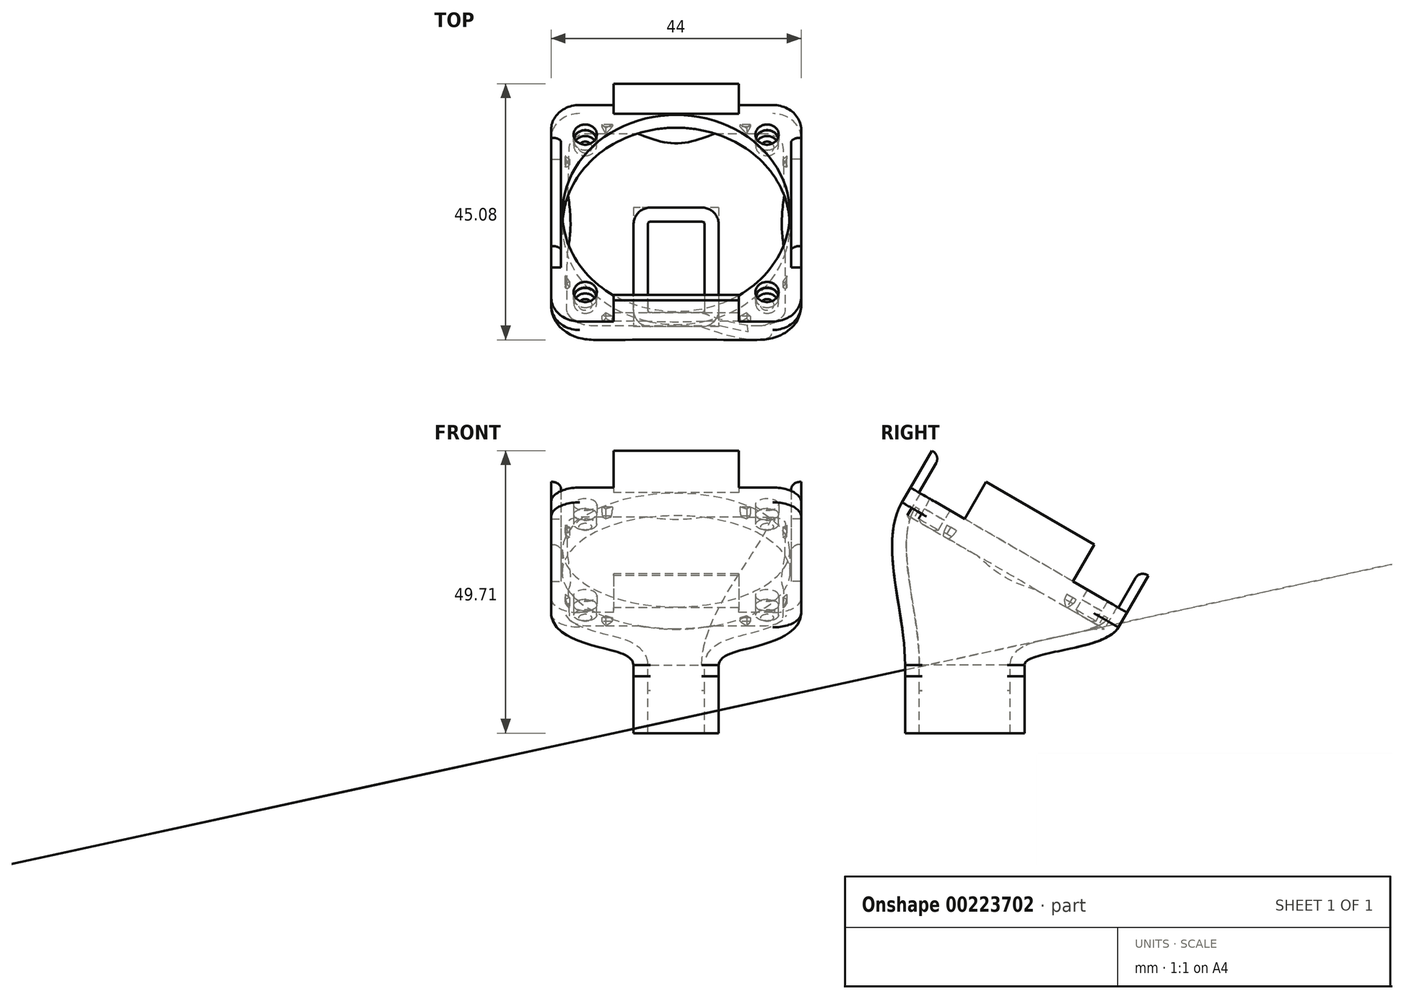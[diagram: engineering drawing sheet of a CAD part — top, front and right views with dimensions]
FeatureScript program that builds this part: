
annotation { "Feature Type Name" : "Feature", "Feature Type Description" : "" }
export const myFeature = defineFeature(function(context is Context, id is Id, definition is map)
    precondition{}
    {
        {
            var Q0;
            Q0=qCreatedBy(makeId("Top.planeOp"),FACE);
            var sketch = newSketch(context, id + "F17", { "sketchPlane" : qUnion([Q0])});
            skLineSegment(sketch, "E0.bottom", {"start": v(7.5, 10.5) * mm, "end": v(-7.5, 10.5) * mm});
            skLineSegment(sketch, "E0.top", {"start": v(7.5, -10.5) * mm, "end": v(-7.5, -10.5) * mm});
            skLineSegment(sketch, "E0.left", {"start": v(7.5, 10.5) * mm, "end": v(7.5, -10.5) * mm});
            skLineSegment(sketch, "E0.right", {"start": v(-7.5, 10.5) * mm, "end": v(-7.5, -10.5) * mm});
            skPoint(sketch, "E0.middle", {"position": v(0, 0) * mm});
            skSolve(sketch);
        }
        {
            var Q0;
            Q0=makeQuery(id+"F17.imprint","IMPRINT",FACE,{"disambiguationData":[TD([[makeQuery(id+"F17.imprint","IMPRINT",EDGE,{"derivedFrom":sQuery(id+"F17.wireOp",EDGE,"E0.bottom")}),1.0]])]});
            extrude(context, id + "F18", {"entities" : qUnion([Q0]), "oppositeDirection" : true, "depth" : 10 * mm});
        }
        {
            var Q0;
            Q0=makeQuery(id+"F18.opExtrude","CAP_FACE",FACE,{"disambiguationData":[OSD([sQuery(id+"F17.wireOp",EDGE,"E0.bottom"),sQuery(id+"F17.wireOp",EDGE,"E0.top"),sQuery(id+"F17.wireOp",EDGE,"E0.left"),sQuery(id+"F17.wireOp",EDGE,"E0.right"),sQuery(id+"F17.wireOp",EDGE,"fad1de10-4d12-4315-86bb-0567689870b4.bottom"),sQuery(id+"F17.wireOp",EDGE,"fad1de10-4d12-4315-86bb-0567689870b4.top"),sQuery(id+"F17.wireOp",EDGE,"fad1de10-4d12-4315-86bb-0567689870b4.left"),sQuery(id+"F17.wireOp",EDGE,"fad1de10-4d12-4315-86bb-0567689870b4.right")])],"isStart":true});
            var sketch = newSketch(context, id + "F0", { "sketchPlane" : qUnion([Q0])});
            skPoint(sketch, "E1.middle", {"position": v(0, 0) * mm});
            skLineSegment(sketch, "E2.bottom", {"start": v(-4.5, -10.5) * mm, "end": v(4.5, -10.5) * mm});
            skLineSegment(sketch, "E2.top", {"start": v(-4.5, 10.5) * mm, "end": v(4.5, 10.5) * mm});
            skLineSegment(sketch, "E2.left", {"start": v(-7.5, -7.5) * mm, "end": v(-7.5, 7.5) * mm});
            skLineSegment(sketch, "E2.right", {"start": v(7.5, -7.5) * mm, "end": v(7.5, 7.5) * mm});
            skPoint(sketch, "E3.visualSharp", {"position": v(-7.5, -10.5) * mm});
            skArc(sketch, "E3.filletArc", {"start": v(-7.5, -7.5) * mm, "mid": v(-6.62, -9.62) * mm, "end": v(-4.5, -10.5) * mm});
            skPoint(sketch, "E4.visualSharp", {"position": v(7.5, -10.5) * mm});
            skArc(sketch, "E4.filletArc", {"start": v(4.5, -10.5) * mm, "mid": v(6.62, -9.62) * mm, "end": v(7.5, -7.5) * mm});
            skPoint(sketch, "E5.visualSharp", {"position": v(7.5, 10.5) * mm});
            skArc(sketch, "E5.filletArc", {"start": v(7.5, 7.5) * mm, "mid": v(6.62, 9.62) * mm, "end": v(4.5, 10.5) * mm});
            skPoint(sketch, "E6.visualSharp", {"position": v(-7.5, 10.5) * mm});
            skArc(sketch, "E6.filletArc", {"start": v(-4.5, 10.5) * mm, "mid": v(-6.62, 9.62) * mm, "end": v(-7.5, 7.5) * mm});
            skSolve(sketch);
        }
        {
            var Q0;
            Q0 = qSketchRegion(id + "F0", true);
            extrude(context, id + "F1", {"entities" : qUnion([Q0]), "operationType" : NewBodyOperationType.ADD, "depth" : 2 * mm});
        }
        {
            var Q0;
            Q0=makeQuery(id+"F1.opExtrude","CAP_FACE",FACE,{"disambiguationData":[OSD([sQuery(id+"F0.wireOp",EDGE,"E1.bottom"),sQuery(id+"F0.wireOp",EDGE,"E1.top"),sQuery(id+"F0.wireOp",EDGE,"E1.left"),sQuery(id+"F0.wireOp",EDGE,"E1.right"),sQuery(id+"F0.wireOp",EDGE,"E2.bottom"),sQuery(id+"F0.wireOp",EDGE,"E2.top"),sQuery(id+"F0.wireOp",EDGE,"E2.left"),sQuery(id+"F0.wireOp",EDGE,"E2.right"),sQuery(id+"F0.wireOp",EDGE,"E3.filletArc"),sQuery(id+"F0.wireOp",EDGE,"E4.filletArc"),sQuery(id+"F0.wireOp",EDGE,"E5.filletArc"),sQuery(id+"F0.wireOp",EDGE,"E6.filletArc")])],"isStart":false});
            cPlane(context, id + "F2", {"entities" : qUnion([Q0]), "cplaneType" : CPlaneType.OFFSET, "offset" : 25 * mm, "width" : 150 * mm, "height" : 150 * mm});
        }
        {
            var Q0;
            Q0=qCreatedBy(id+"F2.planeOp",FACE);
            var Q1;
            Q1=makeQuery(id+"F1.opExtrude","CAP_EDGE",EDGE,{"disambiguationData":[OSD([sQuery(id+"F0.wireOp",EDGE,"E2.top")])],"isStart":false});
            cPlane(context, id + "F3", {"entities" : qUnion([Q0, Q1]), "cplaneType" : CPlaneType.LINE_ANGLE, "offset" : 25 * mm, "angle" : 30 * degree, "width" : 150 * mm, "height" : 150 * mm});
        }
        {
            var Q0;
            Q0=qCreatedBy(id+"F3.planeOp",FACE);
            cPlane(context, id + "F4", {"entities" : qUnion([Q0]), "cplaneType" : CPlaneType.OFFSET, "offset" : 15 * mm, "oppositeDirection" : true, "width" : 150 * mm, "height" : 150 * mm});
        }
        {
            var Q0;
            Q0=qCreatedBy(id+"F4.planeOp",FACE);
            var sketch = newSketch(context, id + "F5", { "sketchPlane" : qUnion([Q0])});
            skLineSegment(sketch, "E7.bottom", {"start": v(17, 24.9) * mm, "end": v(-17, 24.9) * mm});
            skLineSegment(sketch, "E7.top", {"start": v(17, -19.1) * mm, "end": v(-17, -19.1) * mm});
            skLineSegment(sketch, "E7.left", {"start": v(22, 19.9) * mm, "end": v(22, -14.1) * mm});
            skLineSegment(sketch, "E7.right", {"start": v(-22, 19.9) * mm, "end": v(-22, -14.1) * mm});
            skCircle(sketch, "E8", {"center": v(0, 2.9) * mm, "radius": 20 * mm});
            skLineSegment(sketch, "E9.bottom", {"start": v(16, 18.9) * mm, "end": v(-16, 18.9) * mm, "construction": true});
            skLineSegment(sketch, "E9.top", {"start": v(16, -13.1) * mm, "end": v(-16, -13.1) * mm, "construction": true});
            skLineSegment(sketch, "E9.left", {"start": v(16, 18.9) * mm, "end": v(16, -13.1) * mm, "construction": true});
            skLineSegment(sketch, "E9.right", {"start": v(-16, 18.9) * mm, "end": v(-16, -13.1) * mm, "construction": true});
            skCircle(sketch, "E10", {"center": v(16, 18.9) * mm, "radius": 2.05 * mm});
            skCircle(sketch, "E11", {"center": v(-16, 18.9) * mm, "radius": 2.05 * mm});
            skCircle(sketch, "E12", {"center": v(-16, -13.1) * mm, "radius": 2.05 * mm});
            skCircle(sketch, "E13", {"center": v(16, -13.1) * mm, "radius": 2.05 * mm});
            skPoint(sketch, "E14.visualSharp", {"position": v(22, 24.9) * mm});
            skArc(sketch, "E14.filletArc", {"start": v(22, 19.9) * mm, "mid": v(20.54, 23.44) * mm, "end": v(17, 24.9) * mm});
            skPoint(sketch, "E15.visualSharp", {"position": v(-22, 24.9) * mm});
            skArc(sketch, "E15.filletArc", {"start": v(-17, 24.9) * mm, "mid": v(-20.54, 23.44) * mm, "end": v(-22, 19.9) * mm});
            skPoint(sketch, "E16.visualSharp", {"position": v(-22, -19.1) * mm});
            skArc(sketch, "E16.filletArc", {"start": v(-22, -14.1) * mm, "mid": v(-20.54, -17.64) * mm, "end": v(-17, -19.1) * mm});
            skPoint(sketch, "E17.visualSharp", {"position": v(22, -11) * mm});
            skArc(sketch, "E17.filletArc", {"start": v(17, -19.1) * mm, "mid": v(20.54, -17.64) * mm, "end": v(22, -14.1) * mm});
            skSolve(sketch);
        }
        {
            var Q0;
            Q0=makeQuery(id+"F5.imprint","IMPRINT",FACE,{"disambiguationData":[TD([[makeQuery(id+"F5.imprint","IMPRINT",EDGE,{"derivedFrom":sQuery(id+"F5.wireOp",EDGE,"E7.bottom")}),1.0]])]});
            extrude(context, id + "F6", {"entities" : qUnion([Q0]), "operationType" : NewBodyOperationType.ADD, "oppositeDirection" : true, "depth" : 2 * mm});
        }
        {
            var Q0;
            Q0=makeQuery(id+"F6.opExtrude","CAP_FACE",FACE,{"disambiguationData":[OSD([sQuery(id+"F5.wireOp",EDGE,"E7.bottom"),sQuery(id+"F5.wireOp",EDGE,"E7.top"),sQuery(id+"F5.wireOp",EDGE,"E7.left"),sQuery(id+"F5.wireOp",EDGE,"E7.right"),sQuery(id+"F5.wireOp",EDGE,"E8"),sQuery(id+"F5.wireOp",EDGE,"E10"),sQuery(id+"F5.wireOp",EDGE,"E11"),sQuery(id+"F5.wireOp",EDGE,"E12"),sQuery(id+"F5.wireOp",EDGE,"E13"),sQuery(id+"F5.wireOp",EDGE,"E14.filletArc"),sQuery(id+"F5.wireOp",EDGE,"E15.filletArc"),sQuery(id+"F5.wireOp",EDGE,"E16.filletArc"),sQuery(id+"F5.wireOp",EDGE,"E17.filletArc")])],"isStart":false});
            var sketch = newSketch(context, id + "F7", { "sketchPlane" : qUnion([Q0])});
            skLineSegment(sketch, "E18.bottom", {"start": v(22, -13.9) * mm, "end": v(20.25, -13.9) * mm});
            skLineSegment(sketch, "E18.top", {"start": v(22, 8.1) * mm, "end": v(20.25, 8.1) * mm});
            skLineSegment(sketch, "E18.left", {"start": v(22, -13.9) * mm, "end": v(22, 8.1) * mm});
            skLineSegment(sketch, "E18.right", {"start": v(20.25, -13.9) * mm, "end": v(20.25, 8.1) * mm});
            skLineSegment(sketch, "E19", {"start": v(0, -24.9) * mm, "end": v(0, 19.1) * mm, "construction": true});
            skLineSegment(sketch, "E20.MirrorCS", {"start": v(-22, -13.9) * mm, "end": v(-20.25, -13.9) * mm});
            skLineSegment(sketch, "E21.MirrorCS", {"start": v(-20.25, -13.9) * mm, "end": v(-20.25, 8.1) * mm});
            skLineSegment(sketch, "E22.MirrorCS", {"start": v(-22, 8.1) * mm, "end": v(-20.25, 8.1) * mm});
            skLineSegment(sketch, "E23.MirrorCS", {"start": v(-22, -13.9) * mm, "end": v(-22, 8.1) * mm});
            skLineSegment(sketch, "E24.bottom", {"start": v(11, -24.9) * mm, "end": v(-11, -24.9) * mm});
            skLineSegment(sketch, "E24.top", {"start": v(11, -23.15) * mm, "end": v(-11, -23.15) * mm});
            skLineSegment(sketch, "E24.left", {"start": v(11, -24.9) * mm, "end": v(11, -23.15) * mm});
            skLineSegment(sketch, "E24.right", {"start": v(-11, -24.9) * mm, "end": v(-11, -23.15) * mm});
            skLineSegment(sketch, "E25", {"start": v(22, -2.9) * mm, "end": v(-22, -2.9) * mm, "construction": true});
            skLineSegment(sketch, "E26.MirrorCS", {"start": v(11, 17.35) * mm, "end": v(-11, 17.35) * mm});
            skLineSegment(sketch, "E27.MirrorCS", {"start": v(-11, 19.1) * mm, "end": v(-11, 17.35) * mm});
            skLineSegment(sketch, "E28.MirrorCS", {"start": v(11, 19.1) * mm, "end": v(11, 17.35) * mm});
            skLineSegment(sketch, "E29.MirrorCS", {"start": v(11, 19.1) * mm, "end": v(-11, 19.1) * mm});
            skSolve(sketch);
        }
        {
            var Q0;
            Q0=makeQuery(id+"F7.imprint","IMPRINT",FACE,{"disambiguationData":[TD([[makeQuery(id+"F7.imprint","IMPRINT",EDGE,{"derivedFrom":sQuery(id+"F7.wireOp",EDGE,"E18.bottom")}),-1.0]])]});
            var Q1;
            Q1=makeQuery(id+"F7.imprint","IMPRINT",FACE,{"disambiguationData":[TD([[makeQuery(id+"F7.imprint","IMPRINT",EDGE,{"derivedFrom":sQuery(id+"F7.wireOp",EDGE,"E24.bottom")}),-1.0]])]});
            var Q2;
            Q2=makeQuery(id+"F7.imprint","IMPRINT",FACE,{"disambiguationData":[TD([[makeQuery(id+"F7.imprint","IMPRINT",EDGE,{"derivedFrom":sQuery(id+"F7.wireOp",EDGE,"E20.MirrorCS")}),1.0]])]});
            var Q3;
            Q3=makeQuery(id+"F7.imprint","IMPRINT",FACE,{"disambiguationData":[TD([[makeQuery(id+"F7.imprint","IMPRINT",EDGE,{"derivedFrom":sQuery(id+"F7.wireOp",EDGE,"E26.MirrorCS")}),-1.0]])]});
            extrude(context, id + "F8", {"entities" : qUnion([Q0, Q1, Q2, Q3]), "operationType" : NewBodyOperationType.ADD, "depth" : 7.5 * mm});
        }
        {
            var Q0;
            Q0=makeQuery(id+"F8.opExtrude","CAP_EDGE",EDGE,{"disambiguationData":[OSD([sQuery(id+"F7.wireOp",EDGE,"E26.MirrorCS")])],"isStart":false});
            var Q1;
            Q1=makeQuery(id+"F8.opExtrude","CAP_EDGE",EDGE,{"disambiguationData":[OSD([sQuery(id+"F7.wireOp",EDGE,"E21.MirrorCS")])],"isStart":false});
            var Q2;
            Q2=makeQuery(id+"F8.opExtrude","CAP_EDGE",EDGE,{"disambiguationData":[OSD([sQuery(id+"F7.wireOp",EDGE,"E24.top")])],"isStart":false});
            var Q3;
            Q3=makeQuery(id+"F8.opExtrude","CAP_EDGE",EDGE,{"disambiguationData":[OSD([sQuery(id+"F7.wireOp",EDGE,"E18.right")])],"isStart":false});
            fillet(context, id + "F9", {"entities" : qUnion([Q0, Q1, Q2, Q3]), "radius" : 1.5 * mm, "tangentPropagation" : true, "allowEdgeOverflow" : false});
        }
        {
            var Q0;
            Q0=makeQuery(id+"F6.opExtrude","CAP_FACE",FACE,{"disambiguationData":[OSD([sQuery(id+"F5.wireOp",EDGE,"E7.bottom"),sQuery(id+"F5.wireOp",EDGE,"E7.top"),sQuery(id+"F5.wireOp",EDGE,"E7.left"),sQuery(id+"F5.wireOp",EDGE,"E7.right"),sQuery(id+"F5.wireOp",EDGE,"E8"),sQuery(id+"F5.wireOp",EDGE,"E10"),sQuery(id+"F5.wireOp",EDGE,"E11"),sQuery(id+"F5.wireOp",EDGE,"E12"),sQuery(id+"F5.wireOp",EDGE,"E13"),sQuery(id+"F5.wireOp",EDGE,"E14.filletArc"),sQuery(id+"F5.wireOp",EDGE,"E15.filletArc"),sQuery(id+"F5.wireOp",EDGE,"E16.filletArc"),sQuery(id+"F5.wireOp",EDGE,"E17.filletArc")])],"isStart":true});
            cPlane(context, id + "F10", {"entities" : qUnion([Q0]), "cplaneType" : CPlaneType.OFFSET, "offset" : 1 * mm, "width" : 150 * mm, "height" : 150 * mm});
        }
        {
            var Q0;
            Q0=qCreatedBy(id+"F10.planeOp",FACE);
            var sketch = newSketch(context, id + "F11", { "sketchPlane" : qUnion([Q0])});
            skPoint(sketch, "E30", {"position": v(0, 2.9) * mm});
            skLineSegment(sketch, "E31.bottom", {"start": v(-17, 24.9) * mm, "end": v(17, 24.9) * mm});
            skLineSegment(sketch, "E31.top", {"start": v(-17, -19.1) * mm, "end": v(17, -19.1) * mm});
            skLineSegment(sketch, "E31.left", {"start": v(-22, 19.9) * mm, "end": v(-22, -14.1) * mm});
            skLineSegment(sketch, "E31.right", {"start": v(22, 19.9) * mm, "end": v(22, -14.1) * mm});
            skPoint(sketch, "E32.visualSharp", {"position": v(-22, 24.9) * mm});
            skArc(sketch, "E32.filletArc", {"start": v(-17, 24.9) * mm, "mid": v(-20.54, 23.44) * mm, "end": v(-22, 19.9) * mm});
            skPoint(sketch, "E33.visualSharp", {"position": v(22, 24.9) * mm});
            skArc(sketch, "E33.filletArc", {"start": v(22, 19.9) * mm, "mid": v(20.54, 23.44) * mm, "end": v(17, 24.9) * mm});
            skPoint(sketch, "E34.visualSharp", {"position": v(22, -19.1) * mm});
            skArc(sketch, "E34.filletArc", {"start": v(17, -19.1) * mm, "mid": v(20.54, -17.64) * mm, "end": v(22, -14.1) * mm});
            skPoint(sketch, "E35.visualSharp", {"position": v(-22, -19.1) * mm});
            skArc(sketch, "E35.filletArc", {"start": v(-22, -14.1) * mm, "mid": v(-20.54, -17.64) * mm, "end": v(-17, -19.1) * mm});
            skPoint(sketch, "E36.visualSharp", {"position": v(-20, 22.9) * mm});
            skPoint(sketch, "E37.visualSharp", {"position": v(20, 22.9) * mm});
            skPoint(sketch, "E38.visualSharp", {"position": v(20, -17.1) * mm});
            skPoint(sketch, "E39.visualSharp", {"position": v(-20, -17.1) * mm});
            skSolve(sketch);
        }
        {
            var Q0;
            Q0=makeQuery(id+"F11.imprint","IMPRINT",FACE,{"disambiguationData":[TD([[makeQuery(id+"F11.imprint","IMPRINT",EDGE,{"derivedFrom":sQuery(id+"F11.wireOp",EDGE,"E31.bottom")}),-1.0]])]});
            extrude(context, id + "F12", {"entities" : qUnion([Q0]), "operationType" : NewBodyOperationType.ADD, "oppositeDirection" : true, "depth" : 1 * mm});
        }
        {
            var Q0;
            Q0=makeQuery(id+"F1.opExtrude","CAP_FACE",FACE,{"disambiguationData":[OSD([sQuery(id+"F0.wireOp",EDGE,"E2.bottom"),sQuery(id+"F0.wireOp",EDGE,"E2.top"),sQuery(id+"F0.wireOp",EDGE,"E2.left"),sQuery(id+"F0.wireOp",EDGE,"E2.right"),sQuery(id+"F0.wireOp",EDGE,"E3.filletArc"),sQuery(id+"F0.wireOp",EDGE,"E4.filletArc"),sQuery(id+"F0.wireOp",EDGE,"E5.filletArc"),sQuery(id+"F0.wireOp",EDGE,"E6.filletArc")])],"isStart":false});
            var Q1;
            Q1=makeQuery(id+"F12.opExtrude","CAP_FACE",FACE,{"disambiguationData":[OSD([sQuery(id+"F11.wireOp",EDGE,"E31.bottom"),sQuery(id+"F11.wireOp",EDGE,"E31.top"),sQuery(id+"F11.wireOp",EDGE,"E31.left"),sQuery(id+"F11.wireOp",EDGE,"E31.right"),sQuery(id+"F11.wireOp",EDGE,"E32.filletArc"),sQuery(id+"F11.wireOp",EDGE,"E33.filletArc"),sQuery(id+"F11.wireOp",EDGE,"E34.filletArc"),sQuery(id+"F11.wireOp",EDGE,"E35.filletArc")])],"isStart":true});
            loft(context, id + "F13", {"operationType" : NewBodyOperationType.ADD, "startCondition" : LoftEndDerivativeType.NORMAL_TO_PROFILE, "startMagnitude" : 1, "endCondition" : LoftEndDerivativeType.NORMAL_TO_PROFILE, "endMagnitude" : 1, "sheetProfilesArray" : [{ "sheetProfileEntities" : qUnion([Q0]) }, { "sheetProfileEntities" : qUnion([Q1]) }]});
        }
        {
            var Q0;
            Q0=makeQuery(id+"F18.opExtrude","CAP_FACE",FACE,{"disambiguationData":[OSD([sQuery(id+"F17.wireOp",EDGE,"E0.bottom"),sQuery(id+"F17.wireOp",EDGE,"E0.top"),sQuery(id+"F17.wireOp",EDGE,"E0.left"),sQuery(id+"F17.wireOp",EDGE,"E0.right")])],"isStart":false});
            shell(context, id + "F14", {"entities" : qUnion([Q0]), "thickness" : 2.5 * mm});
        }
        {
            var Q0;
            Q0=sQuery(id+"F5.wireOp",VERTEX,"E8.center");
            var Q1;
            Q1=makeQuery(id+"F18.opExtrude","SWEPT_BODY",BODY,{"disambiguationData":[OSD([sQuery(id+"F17.wireOp",EDGE,"E0.bottom"),sQuery(id+"F17.wireOp",EDGE,"E0.top"),sQuery(id+"F17.wireOp",EDGE,"E0.left"),sQuery(id+"F17.wireOp",EDGE,"E0.right")])]});
            hole(context, id + "F15", {"style" : HoleStyle.SIMPLE, "endStyle" : HoleEndStyle.BLIND, "oppositeDirection" : true, "holeDiameter" : 40 * mm, "holeDepth" : 2.5 * mm, "locations" : qUnion([Q0]), "scope" : qUnion([Q1]), "tappedDepth" : 12 * mm, "tapClearance" : 3});
        }
        {
            var Q0;
            Q0=sQuery(id+"F5.wireOp",VERTEX,"E9.top.end");
            var Q1;
            Q1=sQuery(id+"F5.wireOp",VERTEX,"E9.top.start");
            var Q2;
            Q2=sQuery(id+"F5.wireOp",VERTEX,"E9.left.start");
            var Q3;
            Q3=sQuery(id+"F5.wireOp",VERTEX,"E9.bottom.end");
            var Q4;
            Q4=makeQuery(id+"F18.opExtrude","SWEPT_BODY",BODY,{"disambiguationData":[OSD([sQuery(id+"F17.wireOp",EDGE,"E0.bottom"),sQuery(id+"F17.wireOp",EDGE,"E0.top"),sQuery(id+"F17.wireOp",EDGE,"E0.left"),sQuery(id+"F17.wireOp",EDGE,"E0.right")])]});
            hole(context, id + "F16", {"style" : HoleStyle.SIMPLE, "endStyle" : HoleEndStyle.BLIND, "oppositeDirection" : true, "holeDiameter" : 4 * mm, "holeDepth" : 2 * mm, "locations" : qUnion([Q0, Q1, Q2, Q3]), "scope" : qUnion([Q4])});
        }
    });
